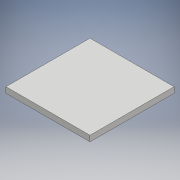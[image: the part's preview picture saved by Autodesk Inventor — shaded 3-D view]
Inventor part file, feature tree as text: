
AUTODESK INVENTOR PART (.ipt)
format: ipt  version: 2018.3 (Build 223284000, 284)  size: 91,648 bytes
history: native  units: mm
features: extrude x1, sketch x1
ambient origin geometry x8: Origin, YZ Plane, XZ Plane, XY Plane, X Axis, Y Axis, Z Axis, Center Point
bodies: Solid1 (feature_tree)
feature tree (2):
  extrude  "Extrusion1"  Depth=14.7mm
  sketch  "Sketch1"  dims[d0=14.7mm d1=14.7mm d2=1.0mm d3=0.0mm]
